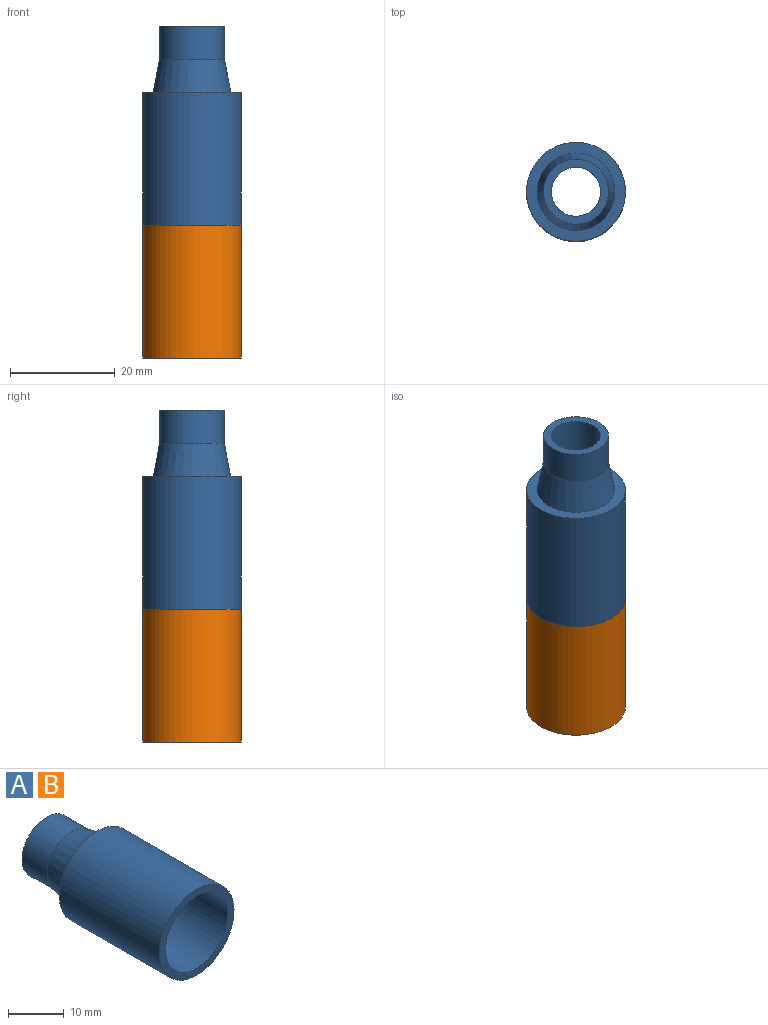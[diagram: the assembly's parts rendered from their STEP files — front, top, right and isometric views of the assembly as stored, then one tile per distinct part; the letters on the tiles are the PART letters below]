
ASSEMBLY  parts=2 mates=1
PART A: 10 faces, bbox 18.9x38.1x18.9 mm
  f0: cylinder r=7.94mm len=23.88mm, axis (0,-1,0), area 1190.8mm2, adj f1,f9
  f1: plane 15.88x15.88mm, normal (0,-1,0), area 78.4mm2, adj f0,f2
  f2: cone r=6.17mm half-angle=10.8deg, axis (0,-1,0), area 268.6mm2, adj f1,f3
  f3: cylinder r=4.7mm len=9.4mm, axis (0,-1,0), area 191.7mm2, adj f2,f4
  f4: plane 12.45x12.45mm, normal (0,1,0), area 52.3mm2, adj f3,f5
  f5: cylinder r=6.22mm len=12.45mm, axis (0,-1,0), area 248.3mm2, adj f4,f6
  f6: cone r=7.43mm half-angle=10.8deg, axis (0,-1,0), area 277.2mm2, adj f5,f7
  f7: plane 18.92x18.92mm, normal (0,1,0), area 107.8mm2, adj f6,f8
  f8: cylinder r=9.46mm len=25.4mm, axis (0,-1,0), area 1510mm2, adj f7,f9
  f9: plane 18.92x18.92mm, normal (0,-1,0), area 83.3mm2, adj f0,f8
PART B: same geometry as A
PLACE A rot(axis=(0.92,-0.28,-0.28),95deg) t=(0,0,25.4)mm
PLACE B rot(axis=(0.8,0.42,0.42),102.5deg) t=(0,0,0)mm
MATE parallel A.f0 <-> B.f0  axis (0,0,-1) through (0,0,25.4)mm
